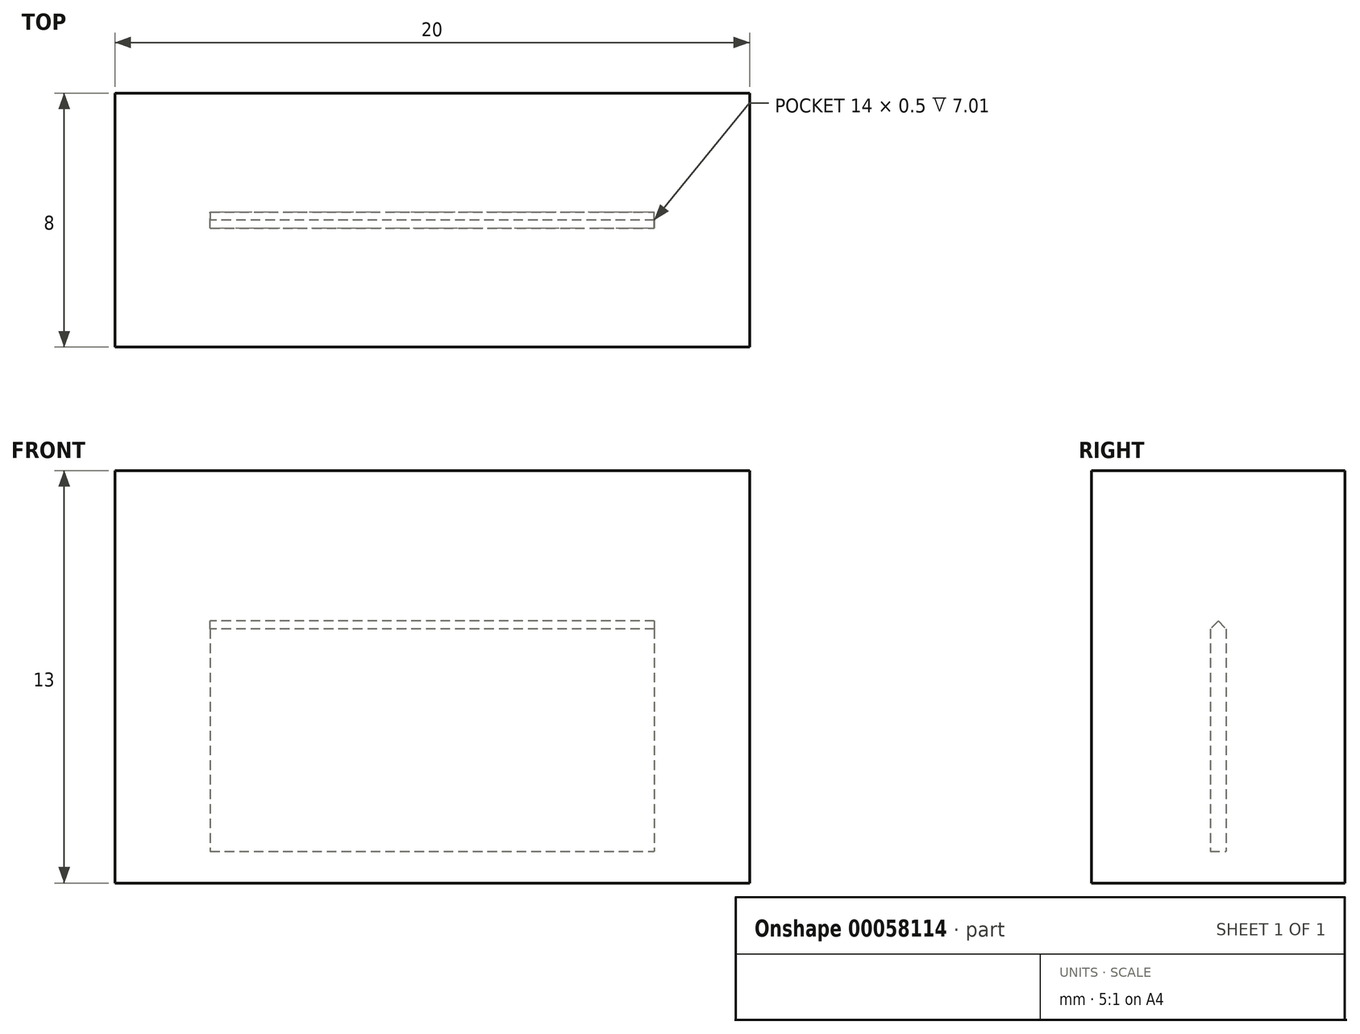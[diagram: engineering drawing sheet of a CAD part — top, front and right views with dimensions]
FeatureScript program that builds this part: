
annotation { "Feature Type Name" : "Feature", "Feature Type Description" : "" }
export const myFeature = defineFeature(function(context is Context, id is Id, definition is map)
    precondition{}
    {
        {
            var Q0;
            Q0=qCreatedBy(makeId("Top.planeOp"),FACE);
            var sketch = newSketch(context, id + "F0", { "sketchPlane" : qUnion([Q0])});
            skLineSegment(sketch, "E0.rect.bottom", {"start": v(10, -4) * mm, "end": v(-10, -4) * mm});
            skLineSegment(sketch, "E0.rect.top", {"start": v(10, 4) * mm, "end": v(-10, 4) * mm});
            skLineSegment(sketch, "E0.rect.left", {"start": v(10, -4) * mm, "end": v(10, 4) * mm});
            skLineSegment(sketch, "E0.rect.right", {"start": v(-10, -4) * mm, "end": v(-10, 4) * mm});
            skPoint(sketch, "E0.rect.middle", {"position": v(0, 0) * mm});
            skSolve(sketch);
        }
        {
            var Q0;
            Q0=makeQuery(id+"F0.imprint","IMPRINT",FACE,{"disambiguationData":[TD([[makeQuery(id+"F0.imprint","IMPRINT",EDGE,{"derivedFrom":sQuery(id+"F0.wireOp",EDGE,"E0.rect.bottom")}),-1.0]])]});
            extrude(context, id + "F1", {"entities" : qUnion([Q0]), "depth" : 1 * mm});
        }
        {
            var Q0;
            Q0=makeQuery(id+"F1.opExtrude","CAP_FACE",FACE,{"disambiguationData":[OSD([sQuery(id+"F0.wireOp",EDGE,"E0.rect.bottom"),sQuery(id+"F0.wireOp",EDGE,"E0.rect.top"),sQuery(id+"F0.wireOp",EDGE,"E0.rect.left"),sQuery(id+"F0.wireOp",EDGE,"E0.rect.right")])],"isStart":false});
            var sketch = newSketch(context, id + "F2", { "sketchPlane" : qUnion([Q0])});
            skLineSegment(sketch, "E1.rect.bottom", {"start": v(-10, -4) * mm, "end": v(10, -4) * mm});
            skLineSegment(sketch, "E1.rect.top", {"start": v(-10, 4) * mm, "end": v(10, 4) * mm});
            skLineSegment(sketch, "E1.rect.left", {"start": v(-10, -4) * mm, "end": v(-10, 4) * mm});
            skLineSegment(sketch, "E1.rect.right", {"start": v(10, -4) * mm, "end": v(10, 4) * mm});
            skPoint(sketch, "E1.rect.middle", {"position": v(0, 0) * mm});
            skLineSegment(sketch, "E2.rect.bottom", {"start": v(-7, -0.25) * mm, "end": v(7, -0.25) * mm});
            skLineSegment(sketch, "E2.rect.top", {"start": v(-7, 0.25) * mm, "end": v(7, 0.25) * mm});
            skLineSegment(sketch, "E2.rect.left", {"start": v(-7, -0.25) * mm, "end": v(-7, 0.25) * mm});
            skLineSegment(sketch, "E2.rect.right", {"start": v(7, -0.25) * mm, "end": v(7, 0.25) * mm});
            skSolve(sketch);
        }
        {
            var Q0;
            Q0=makeQuery(id+"F2.imprint","IMPRINT",FACE,{"disambiguationData":[TD([[makeQuery(id+"F2.imprint","IMPRINT",EDGE,{"derivedFrom":sQuery(id+"F2.wireOp",EDGE,"E1.rect.bottom")}),-1.0]])]});
            extrude(context, id + "F3", {"entities" : qUnion([Q0]), "operationType" : NewBodyOperationType.ADD, "depth" : 10 * mm});
        }
        {
            var Q0;
            Q0=makeQuery(id+"F3.opExtrude","CAP_FACE",FACE,{"disambiguationData":[OSD([sQuery(id+"F2.wireOp",EDGE,"E1.rect.bottom"),sQuery(id+"F2.wireOp",EDGE,"E1.rect.top"),sQuery(id+"F2.wireOp",EDGE,"E1.rect.left"),sQuery(id+"F2.wireOp",EDGE,"E1.rect.right"),sQuery(id+"F2.wireOp",EDGE,"E2.rect.bottom"),sQuery(id+"F2.wireOp",EDGE,"E2.rect.top"),sQuery(id+"F2.wireOp",EDGE,"E2.rect.left"),sQuery(id+"F2.wireOp",EDGE,"E2.rect.right")])],"isStart":false});
            var sketch = newSketch(context, id + "F4", { "sketchPlane" : qUnion([Q0])});
            skLineSegment(sketch, "E3.rect.bottom", {"start": v(-10, 4) * mm, "end": v(10, 4) * mm});
            skLineSegment(sketch, "E3.rect.top", {"start": v(-10, -4) * mm, "end": v(10, -4) * mm});
            skLineSegment(sketch, "E3.rect.left", {"start": v(-10, 4) * mm, "end": v(-10, -4) * mm});
            skLineSegment(sketch, "E3.rect.right", {"start": v(10, 4) * mm, "end": v(10, -4) * mm});
            skPoint(sketch, "E3.rect.middle", {"position": v(0, 0) * mm});
            skSolve(sketch);
        }
        {
            var Q0;
            Q0=makeQuery(id+"F3.opExtrude","SWEPT_FACE",FACE,{"disambiguationData":[OSD([sQuery(id+"F2.wireOp",EDGE,"E2.rect.left")])]});
            var sketch = newSketch(context, id + "F5", { "sketchPlane" : qUnion([Q0])});
            skLineSegment(sketch, "E4", {"start": v(0.25, 8) * mm, "end": v(-2.74, 11) * mm});
            skLineSegment(sketch, "E5", {"start": v(-2.74, 11) * mm, "end": v(0.25, 11) * mm});
            skLineSegment(sketch, "E6", {"start": v(0.25, 11) * mm, "end": v(0.25, 8) * mm});
            skLineSegment(sketch, "E7.MirrorCS", {"start": v(-0.25, 8) * mm, "end": v(2.74, 11) * mm});
            skLineSegment(sketch, "E8.MirrorCS", {"start": v(2.74, 11) * mm, "end": v(-0.25, 11) * mm});
            skLineSegment(sketch, "E9.MirrorCS", {"start": v(-0.25, 11) * mm, "end": v(-0.25, 8) * mm});
            skSolve(sketch);
        }
        {
            var Q0;
            Q0 = qSketchRegion(id + "F5", true);
            var Q1;
            Q1=makeQuery(id+"F3.opExtrude","SWEPT_FACE",FACE,{"disambiguationData":[OSD([sQuery(id+"F2.wireOp",EDGE,"E2.rect.right")])]});
            extrude(context, id + "F6", {"entities" : qUnion([Q0]), "operationType" : NewBodyOperationType.ADD, "endBound" : BoundingType.UP_TO_SURFACE, "endBoundEntityFace" : qUnion([Q1]), "depth" : 25 * mm});
        }
        {
            var Q0;
            Q0=makeQuery(id+"F4.imprint","IMPRINT",FACE,{"disambiguationData":[TD([[makeQuery(id+"F4.imprint","IMPRINT",EDGE,{"derivedFrom":sQuery(id+"F4.wireOp",EDGE,"E3.rect.bottom")}),1.0]])]});
            var sketch = newSketch(context, id + "F7", { "sketchPlane" : qUnion([Q0])});
            skLineSegment(sketch, "E10.rect.bottom", {"start": v(-10, -4) * mm, "end": v(10, -4) * mm});
            skLineSegment(sketch, "E10.rect.top", {"start": v(-10, 4) * mm, "end": v(10, 4) * mm});
            skLineSegment(sketch, "E10.rect.left", {"start": v(-10, -4) * mm, "end": v(-10, 4) * mm});
            skLineSegment(sketch, "E10.rect.right", {"start": v(10, -4) * mm, "end": v(10, 4) * mm});
            skPoint(sketch, "E10.rect.middle", {"position": v(0, 0) * mm});
            skSolve(sketch);
        }
        {
            var Q0;
            Q0 = qSketchRegion(id + "F7", true);
            extrude(context, id + "F8", {"entities" : qUnion([Q0]), "operationType" : NewBodyOperationType.ADD, "depth" : 2 * mm});
        }
    });
